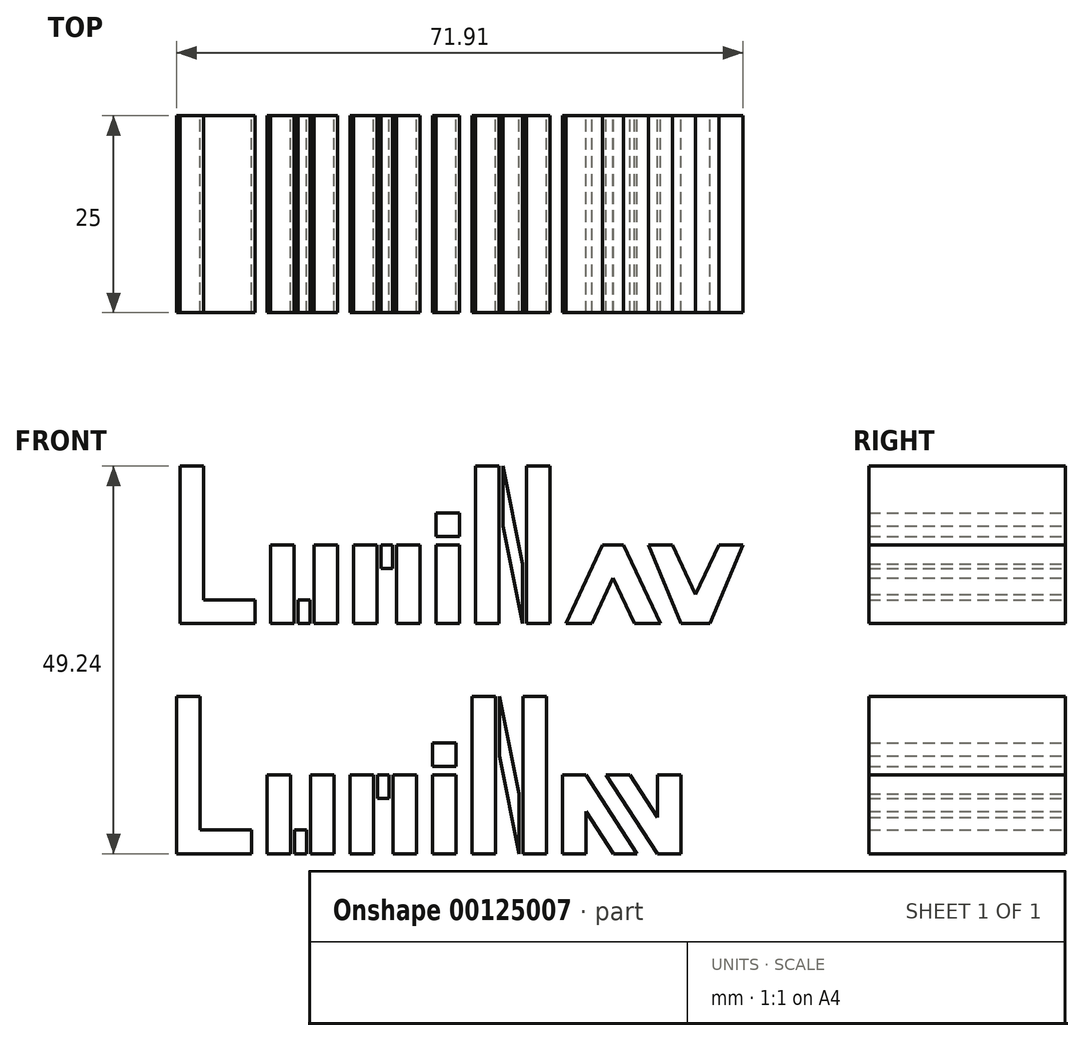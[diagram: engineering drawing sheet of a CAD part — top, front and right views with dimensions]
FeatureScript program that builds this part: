
annotation { "Feature Type Name" : "Feature", "Feature Type Description" : "" }
export const myFeature = defineFeature(function(context is Context, id is Id, definition is map)
    precondition{}
    {
        {
            var Q0;
            Q0=qCreatedBy(makeId("Front.planeOp"),FACE);
            var sketch = newSketch(context, id + "F0", { "sketchPlane" : qUnion([Q0])});
            skLineSegment(sketch, "E0.bottom", {"start": v(-37.5, 20) * mm, "end": v(-34.5, 20) * mm});
            skLineSegment(sketch, "E0.top", {"start": v(-37.5, 0) * mm, "end": v(-34.5, 0) * mm});
            skLineSegment(sketch, "E0.left", {"start": v(-37.5, 20) * mm, "end": v(-37.5, 0) * mm});
            skLineSegment(sketch, "E0.right", {"start": v(-34.5, 20) * mm, "end": v(-34.5, 0) * mm});
            skLineSegment(sketch, "E1.bottom", {"start": v(-34.5, 3) * mm, "end": v(-28, 3) * mm});
            skLineSegment(sketch, "E1.top", {"start": v(-34.5, 0) * mm, "end": v(-28, 0) * mm});
            skLineSegment(sketch, "E1.left", {"start": v(-34.5, 3) * mm, "end": v(-34.5, 0) * mm});
            skLineSegment(sketch, "E1.right", {"start": v(-28, 3) * mm, "end": v(-28, 0) * mm});
            skLineSegment(sketch, "E2.bottom", {"start": v(-26, 10) * mm, "end": v(-23, 10) * mm});
            skLineSegment(sketch, "E2.top", {"start": v(-26, 0) * mm, "end": v(-23, 0) * mm});
            skLineSegment(sketch, "E2.left", {"start": v(-26, 10) * mm, "end": v(-26, 0) * mm});
            skLineSegment(sketch, "E2.right", {"start": v(-23, 10) * mm, "end": v(-23, 0) * mm});
            skLineSegment(sketch, "E3.bottom", {"start": v(-20.5, 10) * mm, "end": v(-17.5, 10) * mm});
            skLineSegment(sketch, "E3.top", {"start": v(-20.5, 0) * mm, "end": v(-17.5, 0) * mm});
            skLineSegment(sketch, "E3.left", {"start": v(-20.5, 10) * mm, "end": v(-20.5, 0) * mm});
            skLineSegment(sketch, "E3.right", {"start": v(-17.5, 10) * mm, "end": v(-17.5, 0) * mm});
            skPoint(sketch, "E4.firstSnap0", {"position": v(-23, 5) * mm});
            skLineSegment(sketch, "E4.top", {"start": v(-23, 0) * mm, "end": v(-20.5, 0) * mm});
            skLineSegment(sketch, "E4.left", {"start": v(-23, 3) * mm, "end": v(-23, 0) * mm});
            skLineSegment(sketch, "E4.right", {"start": v(-20.5, 3) * mm, "end": v(-20.5, 0) * mm});
            skLineSegment(sketch, "E5.bottom", {"start": v(-15.5, 10) * mm, "end": v(-12.5, 10) * mm});
            skLineSegment(sketch, "E5.top", {"start": v(-15.5, 0) * mm, "end": v(-12.5, 0) * mm});
            skLineSegment(sketch, "E5.left", {"start": v(-15.5, 10) * mm, "end": v(-15.5, 0) * mm});
            skLineSegment(sketch, "E5.right", {"start": v(-12.5, 10) * mm, "end": v(-12.5, 0) * mm});
            skLineSegment(sketch, "E6.bottom", {"start": v(-12, 10) * mm, "end": v(-10.5, 10) * mm});
            skLineSegment(sketch, "E6.top", {"start": v(-12, 7) * mm, "end": v(-10.5, 7) * mm});
            skLineSegment(sketch, "E6.left", {"start": v(-12, 10) * mm, "end": v(-12, 7) * mm});
            skLineSegment(sketch, "E6.right", {"start": v(-10.5, 10) * mm, "end": v(-10.5, 7) * mm});
            skLineSegment(sketch, "E7.bottom", {"start": v(-10, 10) * mm, "end": v(-7, 10) * mm});
            skLineSegment(sketch, "E7.top", {"start": v(-10, 0) * mm, "end": v(-7, 0) * mm});
            skLineSegment(sketch, "E7.left", {"start": v(-10, 10) * mm, "end": v(-10, 0) * mm});
            skLineSegment(sketch, "E7.right", {"start": v(-7, 10) * mm, "end": v(-7, 0) * mm});
            skLineSegment(sketch, "E8.bottom", {"start": v(-5, 10) * mm, "end": v(-2, 10) * mm});
            skLineSegment(sketch, "E8.top", {"start": v(-5, 0) * mm, "end": v(-2, 0) * mm});
            skLineSegment(sketch, "E8.left", {"start": v(-5, 10) * mm, "end": v(-5, 0) * mm});
            skLineSegment(sketch, "E8.right", {"start": v(-2, 10) * mm, "end": v(-2, 0) * mm});
            skLineSegment(sketch, "E9.bottom", {"start": v(0, 20) * mm, "end": v(3, 20) * mm});
            skLineSegment(sketch, "E9.top", {"start": v(0, 0) * mm, "end": v(3, 0) * mm});
            skLineSegment(sketch, "E9.left", {"start": v(0, 20) * mm, "end": v(0, 0) * mm});
            skLineSegment(sketch, "E9.right", {"start": v(3, 20) * mm, "end": v(3, 0) * mm});
            skPoint(sketch, "E10.firstSnap0", {"position": v(1.5, 0) * mm});
            skLineSegment(sketch, "E10.bottom", {"start": v(6.5, 0) * mm, "end": v(9.5, 0) * mm});
            skLineSegment(sketch, "E10.top", {"start": v(6.5, 20) * mm, "end": v(9.5, 20) * mm});
            skLineSegment(sketch, "E10.left", {"start": v(6.5, 0) * mm, "end": v(6.5, 20) * mm});
            skLineSegment(sketch, "E10.right", {"start": v(9.5, 0) * mm, "end": v(9.5, 20) * mm});
            skPoint(sketch, "E11.endSnap0", {"position": v(9.5, 10) * mm});
            skLineSegment(sketch, "E12.1", {"start": v(14.81, 0) * mm, "end": v(17.5, 5.77) * mm});
            skLineSegment(sketch, "E13.1", {"start": v(11.5, 0) * mm, "end": v(16.16, 10) * mm});
            skLineSegment(sketch, "E14", {"start": v(17.5, 10) * mm, "end": v(16.16, 10) * mm});
            skLineSegment(sketch, "E15", {"start": v(11.5, 0) * mm, "end": v(14.81, 0) * mm});
            skLineSegment(sketch, "E16.bottom", {"start": v(-22.5, 3) * mm, "end": v(-21, 3) * mm});
            skLineSegment(sketch, "E16.top", {"start": v(-22.5, 0) * mm, "end": v(-21, 0) * mm});
            skLineSegment(sketch, "E16.left", {"start": v(-22.5, 3) * mm, "end": v(-22.5, 0) * mm});
            skLineSegment(sketch, "E16.right", {"start": v(-21, 3) * mm, "end": v(-21, 0) * mm});
            skLineSegment(sketch, "E17", {"start": v(3.5, 12.4) * mm, "end": v(6, 0) * mm});
            skLineSegment(sketch, "E18", {"start": v(3.5, 20) * mm, "end": v(6, 7.6) * mm});
            skLineSegment(sketch, "E19", {"start": v(6, 7.6) * mm, "end": v(6, -7.33) * mm});
            skPoint(sketch, "E20.endSnap0", {"position": v(3, 10) * mm});
            skLineSegment(sketch, "E21", {"start": v(3.5, 20) * mm, "end": v(3.5, 12.4) * mm});
            skLineSegment(sketch, "E22.MirrorCS", {"start": v(21.97, 10) * mm, "end": v(26.14, 0) * mm});
            skLineSegment(sketch, "E23.MirrorCS", {"start": v(25.02, 10) * mm, "end": v(27.97, 3.67) * mm});
            skLineSegment(sketch, "E24", {"start": v(21.97, 10) * mm, "end": v(25.02, 10) * mm});
            skLineSegment(sketch, "E25", {"start": v(27.97, 0) * mm, "end": v(27.97, 13.68) * mm});
            skLineSegment(sketch, "E26", {"start": v(17.5, 10) * mm, "end": v(17.5, 0) * mm});
            skLineSegment(sketch, "E27.MirrorCS", {"start": v(20.19, 0) * mm, "end": v(17.5, 5.77) * mm});
            skLineSegment(sketch, "E28.MirrorCS", {"start": v(23.5, 0) * mm, "end": v(18.84, 10) * mm});
            skLineSegment(sketch, "E29.MirrorCS", {"start": v(23.5, 0) * mm, "end": v(20.19, 0) * mm});
            skLineSegment(sketch, "E30.MirrorCS", {"start": v(17.5, 10) * mm, "end": v(18.84, 10) * mm});
            skLineSegment(sketch, "E31", {"start": v(26.14, 0) * mm, "end": v(27.97, 0) * mm});
            skLineSegment(sketch, "E32.MirrorCS", {"start": v(33.97, 10) * mm, "end": v(29.8, 0) * mm});
            skLineSegment(sketch, "E33.MirrorCS", {"start": v(30.92, 10) * mm, "end": v(27.97, 3.67) * mm});
            skLineSegment(sketch, "E34.MirrorCS", {"start": v(33.97, 10) * mm, "end": v(30.92, 10) * mm});
            skLineSegment(sketch, "E35.MirrorCS", {"start": v(29.8, 0) * mm, "end": v(27.97, 0) * mm});
            skLineSegment(sketch, "E36.bottom", {"start": v(-5, 11.07) * mm, "end": v(-2, 11.07) * mm});
            skLineSegment(sketch, "E36.top", {"start": v(-5, 14.07) * mm, "end": v(-2, 14.07) * mm});
            skLineSegment(sketch, "E36.left", {"start": v(-5, 11.07) * mm, "end": v(-5, 14.07) * mm});
            skLineSegment(sketch, "E36.right", {"start": v(-2, 11.07) * mm, "end": v(-2, 14.07) * mm});
            skPoint(sketch, "E37.endSnap0", {"position": v(13.4, 3.87) * mm});
            skPoint(sketch, "E38.endSnap0", {"position": v(6.9, 3.87) * mm});
            skSolve(sketch);
        }
        {
            var Q0;
            Q0 = qSketchRegion(id + "F0", true);
            extrude(context, id + "F1", {"entities" : qUnion([Q0]), "depth" : 25 * mm});
        }
        {
            var Q0;
            Q0=qCreatedBy(makeId("Front.planeOp"),FACE);
            var sketch = newSketch(context, id + "F2", { "sketchPlane" : qUnion([Q0])});
            skLineSegment(sketch, "E39.bottom", {"start": v(-37.94, -9.24) * mm, "end": v(-34.94, -9.24) * mm});
            skLineSegment(sketch, "E39.top", {"start": v(-37.94, -29.24) * mm, "end": v(-34.94, -29.24) * mm});
            skLineSegment(sketch, "E39.left", {"start": v(-37.94, -9.24) * mm, "end": v(-37.94, -29.24) * mm});
            skLineSegment(sketch, "E39.right", {"start": v(-34.94, -9.24) * mm, "end": v(-34.94, -29.24) * mm});
            skLineSegment(sketch, "E40.bottom", {"start": v(-34.94, -26.24) * mm, "end": v(-28.44, -26.24) * mm});
            skLineSegment(sketch, "E40.top", {"start": v(-34.94, -29.24) * mm, "end": v(-28.44, -29.24) * mm});
            skLineSegment(sketch, "E40.left", {"start": v(-34.94, -26.24) * mm, "end": v(-34.94, -29.24) * mm});
            skLineSegment(sketch, "E40.right", {"start": v(-28.44, -26.24) * mm, "end": v(-28.44, -29.24) * mm});
            skLineSegment(sketch, "E41.bottom", {"start": v(-26.44, -19.24) * mm, "end": v(-23.44, -19.24) * mm});
            skLineSegment(sketch, "E41.top", {"start": v(-26.44, -29.24) * mm, "end": v(-23.44, -29.24) * mm});
            skLineSegment(sketch, "E41.left", {"start": v(-26.44, -19.24) * mm, "end": v(-26.44, -29.24) * mm});
            skLineSegment(sketch, "E41.right", {"start": v(-23.44, -19.24) * mm, "end": v(-23.44, -29.24) * mm});
            skLineSegment(sketch, "E42.bottom", {"start": v(-20.94, -19.24) * mm, "end": v(-17.94, -19.24) * mm});
            skLineSegment(sketch, "E42.top", {"start": v(-20.94, -29.24) * mm, "end": v(-17.94, -29.24) * mm});
            skLineSegment(sketch, "E42.left", {"start": v(-20.94, -19.24) * mm, "end": v(-20.94, -29.24) * mm});
            skLineSegment(sketch, "E42.right", {"start": v(-17.94, -19.24) * mm, "end": v(-17.94, -29.24) * mm});
            skPoint(sketch, "E43.firstSnap0", {"position": v(-23.44, -24.24) * mm});
            skLineSegment(sketch, "E43.top", {"start": v(-23.44, -29.24) * mm, "end": v(-20.94, -29.24) * mm});
            skLineSegment(sketch, "E43.left", {"start": v(-23.44, -26.24) * mm, "end": v(-23.44, -29.24) * mm});
            skLineSegment(sketch, "E44.bottom", {"start": v(-15.94, -19.24) * mm, "end": v(-12.94, -19.24) * mm});
            skLineSegment(sketch, "E44.top", {"start": v(-15.94, -29.24) * mm, "end": v(-12.94, -29.24) * mm});
            skLineSegment(sketch, "E44.left", {"start": v(-15.94, -19.24) * mm, "end": v(-15.94, -29.24) * mm});
            skLineSegment(sketch, "E44.right", {"start": v(-12.94, -19.24) * mm, "end": v(-12.94, -29.24) * mm});
            skLineSegment(sketch, "E45.bottom", {"start": v(-12.44, -19.24) * mm, "end": v(-10.94, -19.24) * mm});
            skLineSegment(sketch, "E45.top", {"start": v(-12.44, -22.24) * mm, "end": v(-10.94, -22.24) * mm});
            skLineSegment(sketch, "E45.left", {"start": v(-12.44, -19.24) * mm, "end": v(-12.44, -22.24) * mm});
            skLineSegment(sketch, "E45.right", {"start": v(-10.94, -19.24) * mm, "end": v(-10.94, -22.24) * mm});
            skLineSegment(sketch, "E46.bottom", {"start": v(-10.44, -19.24) * mm, "end": v(-7.44, -19.24) * mm});
            skLineSegment(sketch, "E46.top", {"start": v(-10.44, -29.24) * mm, "end": v(-7.44, -29.24) * mm});
            skLineSegment(sketch, "E46.left", {"start": v(-10.44, -19.24) * mm, "end": v(-10.44, -29.24) * mm});
            skLineSegment(sketch, "E46.right", {"start": v(-7.44, -19.24) * mm, "end": v(-7.44, -29.24) * mm});
            skLineSegment(sketch, "E47.bottom", {"start": v(-5.44, -19.24) * mm, "end": v(-2.44, -19.24) * mm});
            skLineSegment(sketch, "E47.top", {"start": v(-5.44, -29.24) * mm, "end": v(-2.44, -29.24) * mm});
            skLineSegment(sketch, "E47.left", {"start": v(-5.44, -19.24) * mm, "end": v(-5.44, -29.24) * mm});
            skLineSegment(sketch, "E47.right", {"start": v(-2.44, -19.24) * mm, "end": v(-2.44, -29.24) * mm});
            skLineSegment(sketch, "E48.bottom", {"start": v(-0.44, -9.24) * mm, "end": v(2.56, -9.24) * mm});
            skLineSegment(sketch, "E48.top", {"start": v(-0.44, -29.24) * mm, "end": v(2.56, -29.24) * mm});
            skLineSegment(sketch, "E48.left", {"start": v(-0.44, -9.24) * mm, "end": v(-0.44, -29.24) * mm});
            skLineSegment(sketch, "E48.right", {"start": v(2.56, -9.24) * mm, "end": v(2.56, -29.24) * mm});
            skPoint(sketch, "E49.firstSnap0", {"position": v(1.06, -29.24) * mm});
            skLineSegment(sketch, "E49.bottom", {"start": v(6.06, -29.24) * mm, "end": v(9.06, -29.24) * mm});
            skLineSegment(sketch, "E49.top", {"start": v(6.06, -9.24) * mm, "end": v(9.06, -9.24) * mm});
            skLineSegment(sketch, "E49.left", {"start": v(6.06, -29.24) * mm, "end": v(6.06, -9.24) * mm});
            skLineSegment(sketch, "E49.right", {"start": v(9.06, -29.24) * mm, "end": v(9.06, -9.24) * mm});
            skPoint(sketch, "E50.endSnap0", {"position": v(9.06, -19.24) * mm});
            skLineSegment(sketch, "E51", {"start": v(11.06, -29.24) * mm, "end": v(14.06, -29.24) * mm});
            skLineSegment(sketch, "E52.bottom", {"start": v(-22.94, -26.24) * mm, "end": v(-21.44, -26.24) * mm});
            skLineSegment(sketch, "E52.top", {"start": v(-22.94, -29.24) * mm, "end": v(-21.44, -29.24) * mm});
            skLineSegment(sketch, "E52.left", {"start": v(-22.94, -26.24) * mm, "end": v(-22.94, -29.24) * mm});
            skLineSegment(sketch, "E52.right", {"start": v(-21.44, -26.24) * mm, "end": v(-21.44, -29.24) * mm});
            skLineSegment(sketch, "E53", {"start": v(3.06, -16.83) * mm, "end": v(5.56, -29.24) * mm});
            skLineSegment(sketch, "E54", {"start": v(3.06, -9.24) * mm, "end": v(5.56, -21.65) * mm});
            skLineSegment(sketch, "E55", {"start": v(13.6, -13.45) * mm, "end": v(13.6, -36.8) * mm});
            skPoint(sketch, "E56.endSnap0", {"position": v(2.56, -19.24) * mm});
            skLineSegment(sketch, "E57", {"start": v(3.06, -9.24) * mm, "end": v(3.06, -16.83) * mm});
            skLineSegment(sketch, "E58.bottom", {"start": v(-5.44, -18.17) * mm, "end": v(-2.44, -18.17) * mm});
            skLineSegment(sketch, "E58.top", {"start": v(-5.44, -15.17) * mm, "end": v(-2.44, -15.17) * mm});
            skLineSegment(sketch, "E58.left", {"start": v(-5.44, -18.17) * mm, "end": v(-5.44, -15.17) * mm});
            skLineSegment(sketch, "E58.right", {"start": v(-2.44, -18.17) * mm, "end": v(-2.44, -15.17) * mm});
            skLineSegment(sketch, "E59", {"start": v(5.56, 1.7) * mm, "end": v(5.56, -29.24) * mm});
            skLineSegment(sketch, "E60", {"start": v(11.06, -29.24) * mm, "end": v(11.06, -19.24) * mm});
            skLineSegment(sketch, "E61", {"start": v(14.06, -29.24) * mm, "end": v(14.06, -23.86) * mm});
            skLineSegment(sketch, "E62", {"start": v(14.06, -23.86) * mm, "end": v(17.56, -29.24) * mm});
            skLineSegment(sketch, "E63", {"start": v(11.06, -19.24) * mm, "end": v(14.06, -19.24) * mm});
            skLineSegment(sketch, "E64", {"start": v(14.06, -19.24) * mm, "end": v(20.56, -29.24) * mm});
            skLineSegment(sketch, "E65", {"start": v(17.56, -29.24) * mm, "end": v(20.56, -29.24) * mm});
            skLineSegment(sketch, "E66", {"start": v(16.62, -19.24) * mm, "end": v(23.12, -29.24) * mm});
            skLineSegment(sketch, "E67", {"start": v(16.62, -19.24) * mm, "end": v(19.62, -19.24) * mm});
            skLineSegment(sketch, "E68", {"start": v(23.12, -29.24) * mm, "end": v(26.12, -29.24) * mm});
            skLineSegment(sketch, "E69", {"start": v(26.12, -29.24) * mm, "end": v(26.12, -19.24) * mm});
            skLineSegment(sketch, "E70", {"start": v(26.12, -19.24) * mm, "end": v(23.12, -19.24) * mm});
            skLineSegment(sketch, "E71", {"start": v(23.12, -19.24) * mm, "end": v(23.12, -24.62) * mm});
            skLineSegment(sketch, "E72", {"start": v(19.62, -19.24) * mm, "end": v(23.12, -24.62) * mm});
            skSolve(sketch);
        }
        {
            var Q0;
            Q0 = qSketchRegion(id + "F2", true);
            extrude(context, id + "F3", {"entities" : qUnion([Q0]), "depth" : 25 * mm});
        }
    });
